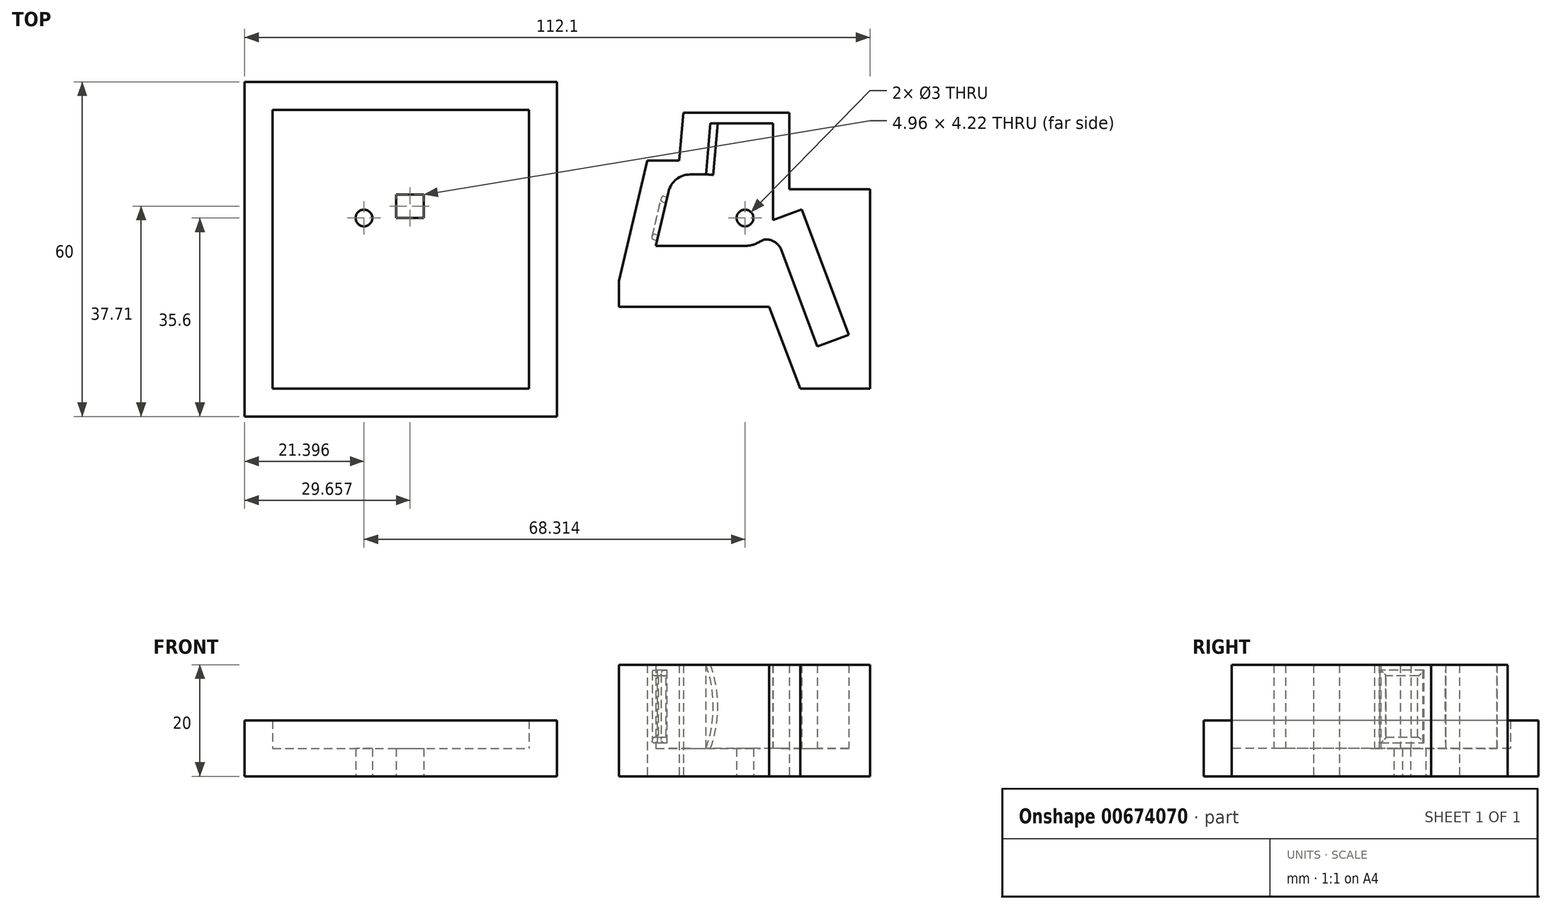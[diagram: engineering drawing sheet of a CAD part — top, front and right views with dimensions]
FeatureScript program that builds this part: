
annotation { "Feature Type Name" : "Feature", "Feature Type Description" : "" }
export const myFeature = defineFeature(function(context is Context, id is Id, definition is map)
    precondition{}
    {
        {
            var Q0;
            Q0=qCreatedBy(makeId("Top.planeOp"),FACE);
            var sketch = newSketch(context, id + "F0", { "sketchPlane" : qUnion([Q0])});
            skLineSegment(sketch, "E0", {"start": v(0, 0) * mm, "end": v(16, 0) * mm});
            skLineSegment(sketch, "E1", {"start": v(21, 4.62) * mm, "end": v(21, 22) * mm});
            skLineSegment(sketch, "E2", {"start": v(21, 22) * mm, "end": v(9.8, 22) * mm});
            skLineSegment(sketch, "E3", {"start": v(6.17, 12.8) * mm, "end": v(9, 12.8) * mm});
            skLineSegment(sketch, "E4", {"start": v(0, 0) * mm, "end": v(2.28, 9.71) * mm});
            skPoint(sketch, "E5.visualSharp", {"position": v(21, 0) * mm});
            skArc(sketch, "E5.filletArc", {"start": v(16, 0) * mm, "mid": v(17.44, 0.21) * mm, "end": v(18.77, 0.84) * mm});
            skPoint(sketch, "E6.visualSharp", {"position": v(19.84, 1.8) * mm});
            skArc(sketch, "E6.filletArc", {"start": v(20.94, 0.86) * mm, "mid": v(19.85, 1.17) * mm, "end": v(18.77, 0.84) * mm});
            skLineSegment(sketch, "E7", {"start": v(9.8, 22) * mm, "end": v(9, 12.8) * mm});
            skPoint(sketch, "E8.visualSharp", {"position": v(3, 12.8) * mm});
            skArc(sketch, "E8.filletArc", {"start": v(6.17, 12.8) * mm, "mid": v(3.69, 11.93) * mm, "end": v(2.28, 9.71) * mm});
            skPoint(sketch, "E9.visualSharp", {"position": v(9, 12.8) * mm});
            skArc(sketch, "E9.filletArc", {"start": v(9, 12.8) * mm, "mid": v(9, 12.8) * mm, "end": v(9, 12.8) * mm});
            skLineSegment(sketch, "E10", {"start": v(26.18, 6.56) * mm, "end": v(34.57, -15.93) * mm});
            skLineSegment(sketch, "E11.0", {"start": v(22.47, -0.65) * mm, "end": v(28.95, -18.02) * mm});
            skLineSegment(sketch, "E12", {"start": v(34.57, -15.93) * mm, "end": v(28.95, -18.02) * mm});
            skLineSegment(sketch, "E13", {"start": v(26.18, 6.56) * mm, "end": v(21, 4.62) * mm});
            skArc(sketch, "E14", {"start": v(22.47, -0.65) * mm, "mid": v(21.87, 0.27) * mm, "end": v(20.94, 0.86) * mm});
            skSolve(sketch);
        }
        {
            var Q0;
            Q0 = qSketchRegion(id + "F0", true);
            extrude(context, id + "F1", {"entities" : qUnion([Q0]), "depth" : 15 * mm, "offsetDistance" : 25 * mm});
        }
        {
            var Q0;
            Q0=makeQuery(id+"F1.opExtrude","SWEPT_FACE",FACE,{"disambiguationData":[OSD([sQuery(id+"F0.wireOp",EDGE,"E7")])]});
            var Q1;
            Q1=makeQuery(id+"F1.opExtrude","SWEPT_EDGE",EDGE,{"disambiguationData":[OSD([sQuery(id+"F0.wireOp",EDGE,"E2"),sQuery(id+"F0.wireOp",EDGE,"E7")])]});
            cPlane(context, id + "F2", {"entities" : qUnion([Q0, Q1]), "cplaneType" : CPlaneType.LINE_ANGLE, "offset" : 25 * mm, "angle" : 90 * degree, "width" : 150 * mm, "height" : 150 * mm});
        }
        {
            var Q0;
            Q0=qCreatedBy(id+"F2.planeOp",FACE);
            var sketch = newSketch(context, id + "F3", { "sketchPlane" : qUnion([Q0])});
            skLineSegment(sketch, "E15", {"start": v(7.86, 0) * mm, "end": v(7.86, 15) * mm});
            skArc(sketch, "E16", {"start": v(7.86, 0) * mm, "mid": v(9.16, 7.5) * mm, "end": v(7.86, 15) * mm});
            skSolve(sketch);
        }
        {
            var Q0;
            Q0 = qSketchRegion(id + "F3", true);
            extrude(context, id + "F4", {"entities" : qUnion([Q0]), "operationType" : NewBodyOperationType.REMOVE, "depth" : 9.2 * mm, "offsetDistance" : 25 * mm, "hasSecondDirection" : true, "secondDirectionOppositeDirection" : true, "secondDirectionDepth" : 1 * mm});
        }
        {
            var Q0;
            Q0=qCreatedBy(makeId("Top.planeOp"),FACE);
            cPlane(context, id + "F5", {"entities" : qUnion([Q0]), "cplaneType" : CPlaneType.OFFSET, "offset" : 5 * mm, "oppositeDirection" : true, "width" : 150 * mm, "height" : 150 * mm});
        }
        {
            var Q0;
            Q0=qCreatedBy(id+"F5.planeOp",FACE);
            var sketch = newSketch(context, id + "F6", { "sketchPlane" : qUnion([Q0])});
            skLineSegment(sketch, "E17.bottom", {"start": v(4.95, 23.9) * mm, "end": v(23.97, 23.9) * mm});
            skLineSegment(sketch, "E17.top", {"start": v(25.93, -25.6) * mm, "end": v(38.4, -25.6) * mm});
            skCircle(sketch, "E18", {"center": v(16, 5) * mm, "radius": 1.5 * mm});
            skLineSegment(sketch, "E19.0", {"start": v(-6.6, -6.28) * mm, "end": v(-6.6, -10.9) * mm});
            skLineSegment(sketch, "E20.0", {"start": v(38.4, 10.14) * mm, "end": v(38.4, -25.6) * mm});
            skLineSegment(sketch, "E21", {"start": v(23.97, 23.9) * mm, "end": v(23.97, 10.14) * mm});
            skLineSegment(sketch, "E22", {"start": v(23.97, 10.14) * mm, "end": v(38.4, 10.14) * mm});
            skLineSegment(sketch, "E23.0", {"start": v(4.95, 23.9) * mm, "end": v(4.2, 15.28) * mm});
            skLineSegment(sketch, "E24", {"start": v(4.2, 15.28) * mm, "end": v(-1.56, 15.28) * mm});
            skLineSegment(sketch, "E25.0", {"start": v(-1.56, 15.28) * mm, "end": v(-6.6, -6.28) * mm});
            skLineSegment(sketch, "E26", {"start": v(-6.6, -10.9) * mm, "end": v(20.34, -10.9) * mm});
            skLineSegment(sketch, "E27", {"start": v(20.34, -10.9) * mm, "end": v(25.93, -25.6) * mm});
            skSolve(sketch);
        }
        {
            var Q0;
            Q0 = qSketchRegion(id + "F6", true);
            extrude(context, id + "F7", {"entities" : qUnion([Q0]), "depth" : 20 * mm, "offsetDistance" : 25 * mm});
        }
        {
            var Q0;
            Q0=makeQuery(id+"F1.opExtrude","SWEPT_BODY",BODY,{"disambiguationData":[OSD([sQuery(id+"F0.wireOp",EDGE,"E0"),sQuery(id+"F0.wireOp",EDGE,"E1"),sQuery(id+"F0.wireOp",EDGE,"E2"),sQuery(id+"F0.wireOp",EDGE,"E3"),sQuery(id+"F0.wireOp",EDGE,"E4"),sQuery(id+"F0.wireOp",EDGE,"HauRUdCC-mjSC-gRyK-8sYp-a8w6gXOHdVk4"),sQuery(id+"F0.wireOp",EDGE,"VMGNVAhK-KKxm-TZSO-n5RP-dL7KX5NL1gEp"),sQuery(id+"F0.wireOp",EDGE,"ViSLpTIR-RkGy-bMqB-4ckY-vp3VoIEgq2xz"),sQuery(id+"F0.wireOp",EDGE,"E5.filletArc"),sQuery(id+"F0.wireOp",EDGE,"hcBzuIZh-c3ar-xEbc-aEu7-VuIi6Doex5UX"),sQuery(id+"F0.wireOp",EDGE,"7461bf76-8539-420d-bea4-f9c92eab774a.trimOffspring"),sQuery(id+"F0.wireOp",EDGE,"827421eb-eac1-4a65-8f9f-ae640561470a.filletArc"),sQuery(id+"F0.wireOp",EDGE,"E6.filletArc"),sQuery(id+"F0.wireOp",EDGE,"E7"),sQuery(id+"F0.wireOp",EDGE,"E8.filletArc"),sQuery(id+"F0.wireOp",EDGE,"E9.filletArc"),sQuery(id+"F0.wireOp",EDGE,"K77RaoLO-KJgs-G7h6-qaX8-02C8ABYDudXd"),sQuery(id+"F0.wireOp",EDGE,"3Nl307vo-Qn71-pQGr-aBtm-efTVCnKNPVXy"),sQuery(id+"F0.wireOp",EDGE,"9291002d-fa5d-4db0-b0a4-c5fa64329f83")])]});
            var Q1;
            Q1=makeQuery(id+"F7.opExtrude","SWEPT_BODY",BODY,{"disambiguationData":[OSD([sQuery(id+"F6.wireOp",EDGE,"E17.bottom"),sQuery(id+"F6.wireOp",EDGE,"E17.top"),sQuery(id+"F6.wireOp",EDGE,"E17.left"),sQuery(id+"F6.wireOp",EDGE,"E17.right")])]});
            booleanBodies(context, id + "F8", {"operationType" : BooleanOperationType.SUBTRACTION, "tools" : qUnion([Q0]), "targets" : qUnion([Q1])});
        }
        {
            var Q0;
            Q0=qCreatedBy(id+"F5.planeOp",FACE);
            var sketch = newSketch(context, id + "F9", { "sketchPlane" : qUnion([Q0])});
            skCircle(sketch, "E28", {"center": v(16, 5) * mm, "radius": 1.5 * mm});
            skSolve(sketch);
        }
        {
            var Q0;
            Q0=makeQuery(id+"F9.imprint","IMPRINT",FACE,{"disambiguationData":[TD([[makeQuery(id+"F9.imprint","IMPRINT",EDGE,{"derivedFrom":sQuery(id+"F9.wireOp",EDGE,"E28")}),1.0]])]});
            extrude(context, id + "F10", {"entities" : qUnion([Q0]), "operationType" : NewBodyOperationType.REMOVE, "depth" : 5 * mm, "offsetDistance" : 25 * mm});
        }
        {
            var Q0;
            Q0=qCreatedBy(id+"F5.planeOp",FACE);
            var sketch = newSketch(context, id + "F11", { "sketchPlane" : qUnion([Q0])});
            skLineSegment(sketch, "E29.bottom", {"start": v(-73.7, -30.6) * mm, "end": v(-17.7, -30.6) * mm});
            skLineSegment(sketch, "E29.top", {"start": v(-73.7, 29.4) * mm, "end": v(-17.7, 29.4) * mm});
            skLineSegment(sketch, "E29.left", {"start": v(-73.7, -30.6) * mm, "end": v(-73.7, 29.4) * mm});
            skLineSegment(sketch, "E29.right", {"start": v(-17.7, -30.6) * mm, "end": v(-17.7, 29.4) * mm});
            skCircle(sketch, "E30", {"center": v(-52.31, 5) * mm, "radius": 1.5 * mm});
            skLineSegment(sketch, "E31.bottom", {"start": v(-46.53, 5) * mm, "end": v(-41.57, 5) * mm});
            skLineSegment(sketch, "E31.top", {"start": v(-46.53, 9.22) * mm, "end": v(-41.57, 9.22) * mm});
            skLineSegment(sketch, "E31.left", {"start": v(-46.53, 5) * mm, "end": v(-46.53, 9.22) * mm});
            skLineSegment(sketch, "E31.right", {"start": v(-41.57, 5) * mm, "end": v(-41.57, 9.22) * mm});
            skSolve(sketch);
        }
        {
            var Q0;
            Q0=makeQuery(id+"F11.imprint","IMPRINT",FACE,{"disambiguationData":[TD([[makeQuery(id+"F11.imprint","IMPRINT",EDGE,{"derivedFrom":sQuery(id+"F11.wireOp",EDGE,"E29.bottom")}),1.0]])]});
            extrude(context, id + "F12", {"entities" : qUnion([Q0]), "depth" : 5 * mm, "offsetDistance" : 25 * mm});
        }
        {
            var Q0;
            Q0=makeQuery(id+"F12.opExtrude","CAP_FACE",FACE,{"disambiguationData":[OSD([sQuery(id+"F11.wireOp",EDGE,"E29.bottom"),sQuery(id+"F11.wireOp",EDGE,"E29.top"),sQuery(id+"F11.wireOp",EDGE,"E29.left"),sQuery(id+"F11.wireOp",EDGE,"E29.right"),sQuery(id+"F11.wireOp",EDGE,"E30")])],"isStart":false});
            cPlane(context, id + "F13", {"entities" : qUnion([Q0]), "cplaneType" : CPlaneType.OFFSET, "offset" : 0 * mm, "width" : 150 * mm, "height" : 150 * mm});
        }
        {
            var Q0;
            Q0=qCreatedBy(id+"F13.planeOp",FACE);
            var sketch = newSketch(context, id + "F14", { "sketchPlane" : qUnion([Q0])});
            skLineSegment(sketch, "E32.bottom", {"start": v(-73.7, 29.4) * mm, "end": v(-17.7, 29.4) * mm});
            skLineSegment(sketch, "E32.top", {"start": v(-73.7, -30.6) * mm, "end": v(-17.7, -30.6) * mm});
            skLineSegment(sketch, "E32.left", {"start": v(-73.7, 29.4) * mm, "end": v(-73.7, -30.6) * mm});
            skLineSegment(sketch, "E32.right", {"start": v(-17.7, 29.4) * mm, "end": v(-17.7, -30.6) * mm});
            skLineSegment(sketch, "E33.0", {"start": v(-68.7, 24.4) * mm, "end": v(-22.7, 24.4) * mm});
            skLineSegment(sketch, "E33.1", {"start": v(-68.7, 24.4) * mm, "end": v(-68.7, -25.6) * mm});
            skLineSegment(sketch, "E33.2", {"start": v(-68.7, -25.6) * mm, "end": v(-22.7, -25.6) * mm});
            skLineSegment(sketch, "E33.3", {"start": v(-22.7, 24.4) * mm, "end": v(-22.7, -25.6) * mm});
            skSolve(sketch);
        }
        {
            var Q0;
            Q0=makeQuery(id+"F14.imprint","IMPRINT",FACE,{"disambiguationData":[TD([[makeQuery(id+"F14.imprint","IMPRINT",EDGE,{"derivedFrom":sQuery(id+"F14.wireOp",EDGE,"E32.bottom")}),-1.0]])]});
            extrude(context, id + "F15", {"entities" : qUnion([Q0]), "operationType" : NewBodyOperationType.ADD, "depth" : 5 * mm, "offsetDistance" : 25 * mm});
        }
        {
            var Q0;
            Q0=qCreatedBy(makeId("Right.planeOp"),FACE);
            cPlane(context, id + "F16", {"entities" : qUnion([Q0]), "cplaneType" : CPlaneType.OFFSET, "offset" : 88 * mm, "oppositeDirection" : true, "width" : 150 * mm, "height" : 150 * mm});
        }
        {
            var Q0;
            Q0=qCreatedBy(id+"F16.planeOp",FACE);
            var sketch = newSketch(context, id + "F17", { "sketchPlane" : qUnion([Q0])});
            skCircle(sketch, "E34", {"center": v(0, 0) * mm, "radius": 2.25 * mm});
            skSolve(sketch);
        }
        {
            var Q0;
            Q0=sQuery(id+"F17.wireOp",EDGE,"E34");
            extrude(context, id + "F18", {"bodyType" : ExtendedToolBodyType.SURFACE, "surfaceEntities" : qUnion([Q0]), "oppositeDirection" : true, "depth" : 25 * mm, "offsetDistance" : 25 * mm});
        }
        {
            var Q0;
            Q0=makeQuery(id+"F8.opBoolean","COPY",FACE,{"derivedFrom":makeQuery(id+"F1.opExtrude","SWEPT_FACE",FACE,{"disambiguationData":[OSD([sQuery(id+"F0.wireOp",EDGE,"E4")])]})});
            cPlane(context, id + "F19", {"entities" : qUnion([Q0]), "cplaneType" : CPlaneType.OFFSET, "offset" : 0 * mm, "width" : 150 * mm, "height" : 150 * mm});
        }
        {
            var Q0;
            Q0=qCreatedBy(id+"F19.planeOp",FACE);
            var sketch = newSketch(context, id + "F20", { "sketchPlane" : qUnion([Q0])});
            skLineSegment(sketch, "E35.0", {"start": v(1, 1) * mm, "end": v(8.98, 1) * mm});
            skLineSegment(sketch, "E35.1", {"start": v(1, 14) * mm, "end": v(1, 1) * mm});
            skLineSegment(sketch, "E35.2", {"start": v(8.98, 14) * mm, "end": v(1, 14) * mm});
            skLineSegment(sketch, "E35.3", {"start": v(8.98, 1) * mm, "end": v(8.98, 14) * mm});
            skLineSegment(sketch, "E36.0", {"start": v(2, 2) * mm, "end": v(7.98, 2) * mm});
            skLineSegment(sketch, "E36.1", {"start": v(2, 13) * mm, "end": v(2, 2) * mm});
            skLineSegment(sketch, "E36.2", {"start": v(7.98, 13) * mm, "end": v(2, 13) * mm});
            skLineSegment(sketch, "E36.3", {"start": v(7.98, 2) * mm, "end": v(7.98, 13) * mm});
            skSolve(sketch);
        }
        {
            var Q0;
            Q0=makeQuery(id+"F20.imprint","IMPRINT",FACE,{"disambiguationData":[TD([[makeQuery(id+"F20.imprint","IMPRINT",EDGE,{"derivedFrom":sQuery(id+"F20.wireOp",EDGE,"E35.0")}),1.0]])]});
            extrude(context, id + "F21", {"entities" : qUnion([Q0]), "operationType" : NewBodyOperationType.REMOVE, "oppositeDirection" : true, "depth" : 1 * mm, "offsetDistance" : 25 * mm});
        }
        {
            var Q0;
            Q0=makeQuery(id+"F21.boolean.opBoolean","COPY",EDGE,{"derivedFrom":makeQuery(id+"F21.opExtrude","CAP_EDGE",EDGE,{"disambiguationData":[OSD([sQuery(id+"F20.wireOp",EDGE,"E35.3")])],"isStart":false})});
            var Q1;
            Q1=makeQuery(id+"F21.boolean.opBoolean","COPY",EDGE,{"derivedFrom":makeQuery(id+"F21.opExtrude","CAP_EDGE",EDGE,{"disambiguationData":[OSD([sQuery(id+"F20.wireOp",EDGE,"E35.2")])],"isStart":false})});
            var Q2;
            Q2=makeQuery(id+"F21.boolean.opBoolean","COPY",EDGE,{"derivedFrom":makeQuery(id+"F21.opExtrude","CAP_EDGE",EDGE,{"disambiguationData":[OSD([sQuery(id+"F20.wireOp",EDGE,"E35.1")])],"isStart":false})});
            var Q3;
            Q3=makeQuery(id+"F21.boolean.opBoolean","COPY",EDGE,{"derivedFrom":makeQuery(id+"F21.opExtrude","CAP_EDGE",EDGE,{"disambiguationData":[OSD([sQuery(id+"F20.wireOp",EDGE,"E35.0")])],"isStart":false})});
            var Q4;
            Q4=makeQuery(id+"F21.boolean.opBoolean","COPY",EDGE,{"derivedFrom":makeQuery(id+"F21.opExtrude","CAP_EDGE",EDGE,{"disambiguationData":[OSD([sQuery(id+"F20.wireOp",EDGE,"E36.3")])],"isStart":false})});
            var Q5;
            Q5=makeQuery(id+"F21.boolean.opBoolean","COPY",EDGE,{"derivedFrom":makeQuery(id+"F21.opExtrude","CAP_EDGE",EDGE,{"disambiguationData":[OSD([sQuery(id+"F20.wireOp",EDGE,"E36.2")])],"isStart":false})});
            var Q6;
            Q6=makeQuery(id+"F21.boolean.opBoolean","COPY",EDGE,{"derivedFrom":makeQuery(id+"F21.opExtrude","CAP_EDGE",EDGE,{"disambiguationData":[OSD([sQuery(id+"F20.wireOp",EDGE,"E36.1")])],"isStart":false})});
            var Q7;
            Q7=makeQuery(id+"F21.boolean.opBoolean","COPY",EDGE,{"derivedFrom":makeQuery(id+"F21.opExtrude","CAP_EDGE",EDGE,{"disambiguationData":[OSD([sQuery(id+"F20.wireOp",EDGE,"E36.0")])],"isStart":false})});
            fillet(context, id + "F22", {"entities" : qUnion([Q0, Q1, Q2, Q3, Q4, Q5, Q6, Q7]), "radius" : .4 * mm, "tangentPropagation" : true, "allowEdgeOverflow" : false});
        }
    });
